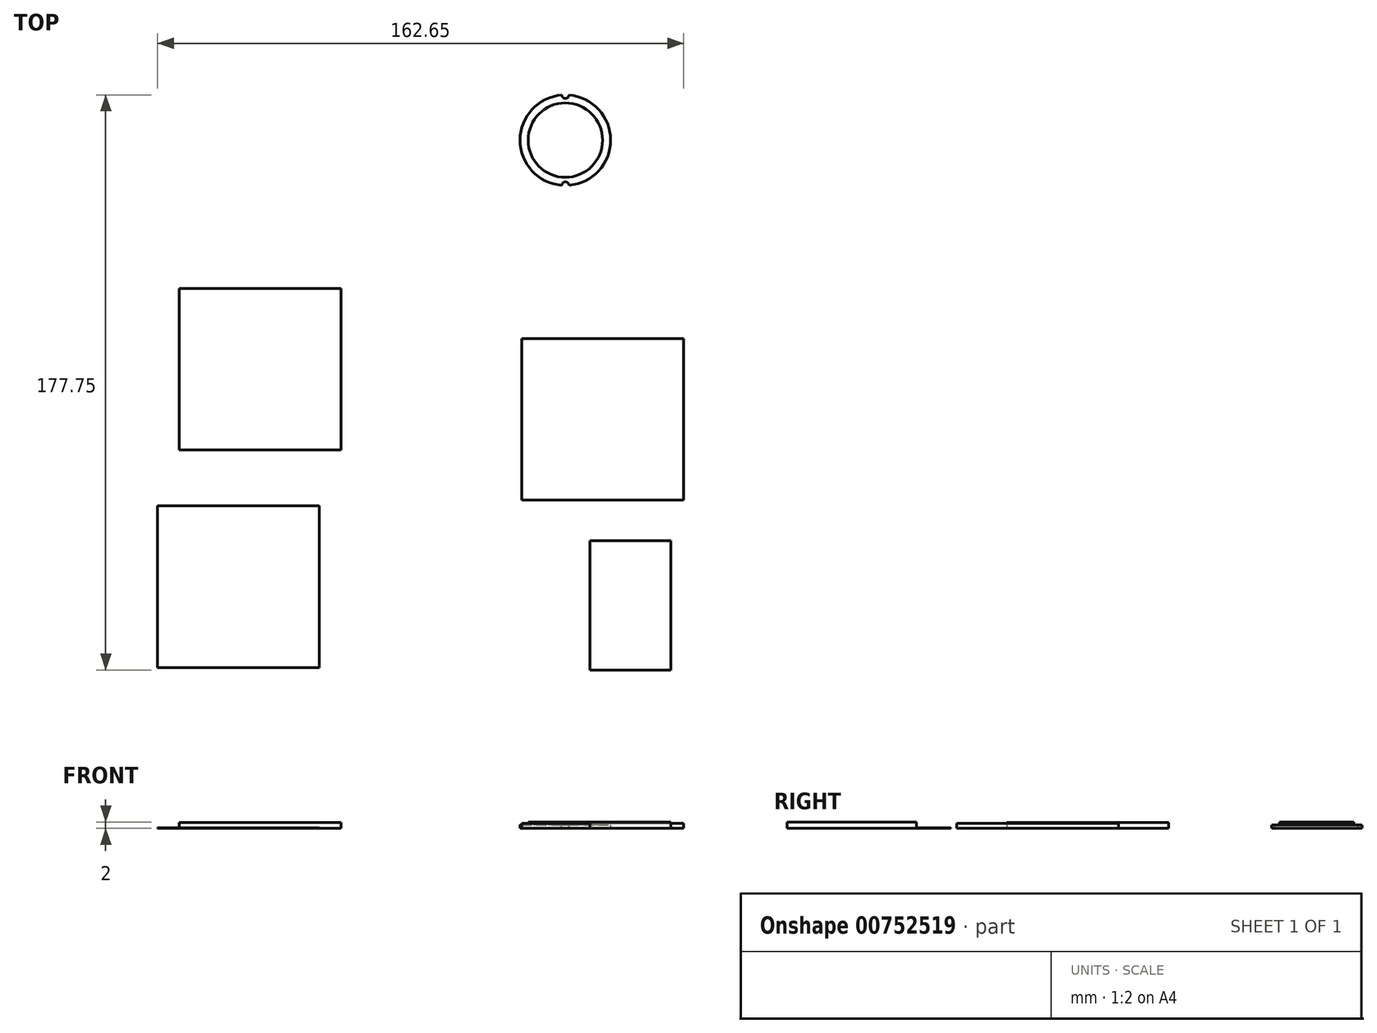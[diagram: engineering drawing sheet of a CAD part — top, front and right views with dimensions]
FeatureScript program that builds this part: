
annotation { "Feature Type Name" : "Feature", "Feature Type Description" : "" }
export const myFeature = defineFeature(function(context is Context, id is Id, definition is map)
    precondition{}
    {
        {
            var Q0;
            Q0=qCreatedBy(makeId("Top.planeOp"),FACE);
            var sketch = newSketch(context, id + "F0", { "sketchPlane" : qUnion([Q0])});
            skLineSegment(sketch, "E0.bottom", {"start": v(-85.47, 38.03) * mm, "end": v(-35.47, 38.03) * mm});
            skLineSegment(sketch, "E0.top", {"start": v(-85.47, -11.97) * mm, "end": v(-35.47, -11.97) * mm});
            skLineSegment(sketch, "E0.left", {"start": v(-85.47, 38.03) * mm, "end": v(-85.47, -11.97) * mm});
            skLineSegment(sketch, "E0.right", {"start": v(-35.47, 38.03) * mm, "end": v(-35.47, -11.97) * mm});
            skLineSegment(sketch, "E1.bottom", {"start": v(20.45, 22.55) * mm, "end": v(70.45, 22.55) * mm});
            skLineSegment(sketch, "E1.top", {"start": v(20.45, -27.45) * mm, "end": v(70.45, -27.45) * mm});
            skLineSegment(sketch, "E1.left", {"start": v(20.45, 22.55) * mm, "end": v(20.45, -27.45) * mm});
            skLineSegment(sketch, "E1.right", {"start": v(70.45, 22.55) * mm, "end": v(70.45, -27.45) * mm});
            skLineSegment(sketch, "E2.bottom", {"start": v(-92.2, -29.22) * mm, "end": v(-42.2, -29.22) * mm});
            skLineSegment(sketch, "E2.top", {"start": v(-92.2, -79.22) * mm, "end": v(-42.2, -79.22) * mm});
            skLineSegment(sketch, "E2.left", {"start": v(-92.2, -29.22) * mm, "end": v(-92.2, -79.22) * mm});
            skLineSegment(sketch, "E2.right", {"start": v(-42.2, -29.22) * mm, "end": v(-42.2, -79.22) * mm});
            skLineSegment(sketch, "E3.bottom", {"start": v(41.54, -39.93) * mm, "end": v(66.54, -39.93) * mm});
            skLineSegment(sketch, "E3.top", {"start": v(41.54, -79.93) * mm, "end": v(66.54, -79.93) * mm});
            skLineSegment(sketch, "E3.left", {"start": v(41.54, -39.93) * mm, "end": v(41.54, -79.93) * mm});
            skLineSegment(sketch, "E3.right", {"start": v(66.54, -39.93) * mm, "end": v(66.54, -79.93) * mm});
            skCircle(sketch, "E4", {"center": v(33.88, 83.86) * mm, "radius": 14 * mm});
            skCircle(sketch, "E5", {"center": v(33.88, 83.86) * mm, "radius": 11.5 * mm});
            skPoint(sketch, "E6", {"position": v(33.88, 97.86) * mm});
            skPoint(sketch, "E7", {"position": v(33.88, 69.86) * mm});
            skSolve(sketch);
        }
        {
            var Q0;
            Q0=makeQuery(id+"F0.imprint","IMPRINT",FACE,{"disambiguationData":[TD([[makeQuery(id+"F0.imprint","IMPRINT",EDGE,{"derivedFrom":sQuery(id+"F0.wireOp",EDGE,"E0.bottom")}),-1.0]])]});
            extrude(context, id + "F1", {"entities" : qUnion([Q0]), "depth" : 1.78 * mm, "offsetDistance" : 25 * mm});
        }
        {
            var Q0;
            Q0=makeQuery(id+"F0.imprint","IMPRINT",FACE,{"disambiguationData":[TD([[makeQuery(id+"F0.imprint","IMPRINT",EDGE,{"derivedFrom":sQuery(id+"F0.wireOp",EDGE,"E1.bottom")}),-1.0]])]});
            extrude(context, id + "F2", {"entities" : qUnion([Q0]), "depth" : 1.6 * mm, "offsetDistance" : 25 * mm});
        }
        {
            var Q0;
            Q0=makeQuery(id+"F0.imprint","IMPRINT",FACE,{"disambiguationData":[TD([[makeQuery(id+"F0.imprint","IMPRINT",EDGE,{"derivedFrom":sQuery(id+"F0.wireOp",EDGE,"E2.bottom")}),-1.0]])]});
            extrude(context, id + "F3", {"entities" : qUnion([Q0]), "depth" : .2 * mm, "offsetDistance" : 25 * mm});
        }
        {
            var Q0;
            Q0=makeQuery(id+"F0.imprint","IMPRINT",FACE,{"disambiguationData":[TD([[makeQuery(id+"F0.imprint","IMPRINT",EDGE,{"derivedFrom":sQuery(id+"F0.wireOp",EDGE,"E3.bottom")}),-1.0]])]});
            extrude(context, id + "F4", {"entities" : qUnion([Q0]), "depth" : 2 * mm, "offsetDistance" : 25 * mm});
        }
        {
            var Q0;
            Q0=makeQuery(id+"F0.imprint","IMPRINT",FACE,{"disambiguationData":[TD([[makeQuery(id+"F0.imprint","IMPRINT",EDGE,{"derivedFrom":sQuery(id+"F0.wireOp",EDGE,"E5")}),1.0]])]});
            extrude(context, id + "F5", {"entities" : qUnion([Q0]), "depth" : 2 * mm, "offsetDistance" : 25 * mm});
        }
        {
            var Q0;
            Q0=makeQuery(id+"F0.imprint","IMPRINT",FACE,{"disambiguationData":[TD([[makeQuery(id+"F0.imprint","IMPRINT",EDGE,{"derivedFrom":sQuery(id+"F0.wireOp",EDGE,"E4")}),1.0]])]});
            extrude(context, id + "F6", {"entities" : qUnion([Q0]), "operationType" : NewBodyOperationType.ADD, "depth" : 1 * mm, "offsetDistance" : 25 * mm});
        }
        {
            var Q0;
            Q0=sQuery(id+"F0.wireOp",VERTEX,"E6");
            var Q1;
            Q1=sQuery(id+"F0.wireOp",VERTEX,"E7");
            var Q2;
            Q2=makeQuery(id+"F5.opExtrude","SWEPT_BODY",BODY,{"disambiguationData":[OSD([sQuery(id+"F0.wireOp",EDGE,"E5")])]});
            hole(context, id + "F7", {"style" : HoleStyle.SIMPLE, "endStyle" : HoleEndStyle.THROUGH, "oppositeDirection" : true, "holeDiameter" : 2.2 * mm, "majorDiameter" : 5 * mm, "isTappedThrough" : true, "tappedDepth" : 12 * mm, "tapClearance" : 3, "locations" : qUnion([Q0, Q1]), "scope" : qUnion([Q2]), "startStyle" : HoleStartStyle.PART});
        }
    });
